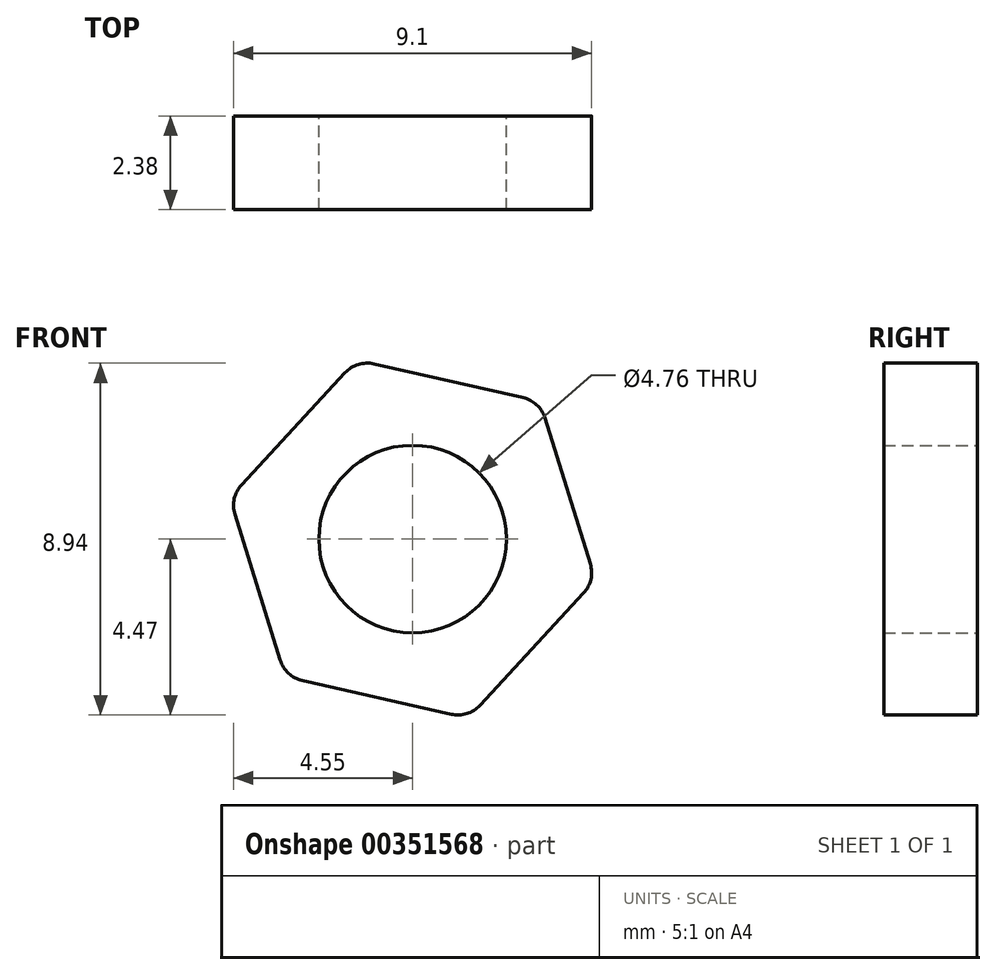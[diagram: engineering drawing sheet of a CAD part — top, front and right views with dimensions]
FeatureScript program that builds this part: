
annotation { "Feature Type Name" : "Feature", "Feature Type Description" : "" }
export const myFeature = defineFeature(function(context is Context, id is Id, definition is map)
    precondition{}
    {
        {
            var Q0;
            Q0=qCreatedBy(makeId("Front.planeOp"),FACE);
            var sketch = newSketch(context, id + "F0", { "sketchPlane" : qUnion([Q0])});
            skCircle(sketch, "E0.cCircle", {"center": v(0, 0) * mm, "radius": 4.12 * mm, "construction": true});
            skLineSegment(sketch, "E0.0", {"start": v(-4.65, 1.05) * mm, "end": v(-1.41, 4.55) * mm});
            skLineSegment(sketch, "E0.1", {"start": v(-1.41, 4.55) * mm, "end": v(3.23, 3.5) * mm});
            skLineSegment(sketch, "E0.2", {"start": v(3.23, 3.5) * mm, "end": v(4.65, -1.05) * mm});
            skLineSegment(sketch, "E0.3", {"start": v(4.65, -1.05) * mm, "end": v(1.41, -4.55) * mm});
            skLineSegment(sketch, "E0.4", {"start": v(1.41, -4.55) * mm, "end": v(-3.23, -3.5) * mm});
            skLineSegment(sketch, "E0.5", {"start": v(-3.23, -3.5) * mm, "end": v(-4.65, 1.05) * mm});
            skPoint(sketch, "E0.0.midPoint", {"position": v(-3.03, 2.8) * mm});
            skSolve(sketch);
        }
        {
            var Q0;
            Q0 = qSketchRegion(id + "F0", true);
            extrude(context, id + "F1", {"entities" : qUnion([Q0]), "depth" : 2.38 * mm, "symmetric" : true});
        }
        {
            var Q0;
            Q0=makeQuery(id+"F1.opExtrude","CAP_FACE",FACE,{"disambiguationData":[OSD([sQuery(id+"F0.wireOp",EDGE,"E0.0"),sQuery(id+"F0.wireOp",EDGE,"E0.1"),sQuery(id+"F0.wireOp",EDGE,"E0.2"),sQuery(id+"F0.wireOp",EDGE,"E0.3"),sQuery(id+"F0.wireOp",EDGE,"E0.4"),sQuery(id+"F0.wireOp",EDGE,"E0.5")])],"isStart":true});
            var sketch = newSketch(context, id + "F2", { "sketchPlane" : qUnion([Q0])});
            skCircle(sketch, "E1", {"center": v(0, 0) * mm, "radius": 2.38 * mm});
            skSolve(sketch);
        }
        {
            var Q0;
            Q0 = qSketchRegion(id + "F2", true);
            extrude(context, id + "F3", {"entities" : qUnion([Q0]), "operationType" : NewBodyOperationType.REMOVE, "oppositeDirection" : true, "depth" : 2.38 * mm});
        }
        {
            var Q0;
            Q0=makeQuery(id+"F1.opExtrude","SWEPT_EDGE",EDGE,{"disambiguationData":[OSD([sQuery(id+"F0.wireOp",EDGE,"E0.0"),sQuery(id+"F0.wireOp",EDGE,"E0.1")])]});
            var Q1;
            Q1=makeQuery(id+"F1.opExtrude","SWEPT_EDGE",EDGE,{"disambiguationData":[OSD([sQuery(id+"F0.wireOp",EDGE,"E0.1"),sQuery(id+"F0.wireOp",EDGE,"E0.2")])]});
            var Q2;
            Q2=makeQuery(id+"F1.opExtrude","SWEPT_EDGE",EDGE,{"disambiguationData":[OSD([sQuery(id+"F0.wireOp",EDGE,"E0.2"),sQuery(id+"F0.wireOp",EDGE,"E0.3")])]});
            var Q3;
            Q3=makeQuery(id+"F1.opExtrude","SWEPT_EDGE",EDGE,{"disambiguationData":[OSD([sQuery(id+"F0.wireOp",EDGE,"E0.3"),sQuery(id+"F0.wireOp",EDGE,"E0.4")])]});
            var Q4;
            Q4=makeQuery(id+"F1.opExtrude","SWEPT_EDGE",EDGE,{"disambiguationData":[OSD([sQuery(id+"F0.wireOp",EDGE,"E0.4"),sQuery(id+"F0.wireOp",EDGE,"E0.5")])]});
            var Q5;
            Q5=makeQuery(id+"F1.opExtrude","SWEPT_EDGE",EDGE,{"disambiguationData":[OSD([sQuery(id+"F0.wireOp",EDGE,"E0.0"),sQuery(id+"F0.wireOp",EDGE,"E0.5")])]});
            fillet(context, id + "F4", {"entities" : qUnion([Q0, Q1, Q2, Q3, Q4, Q5]), "radius" : 0.76 * mm, "tangentPropagation" : true, "allowEdgeOverflow" : false});
        }
    });
